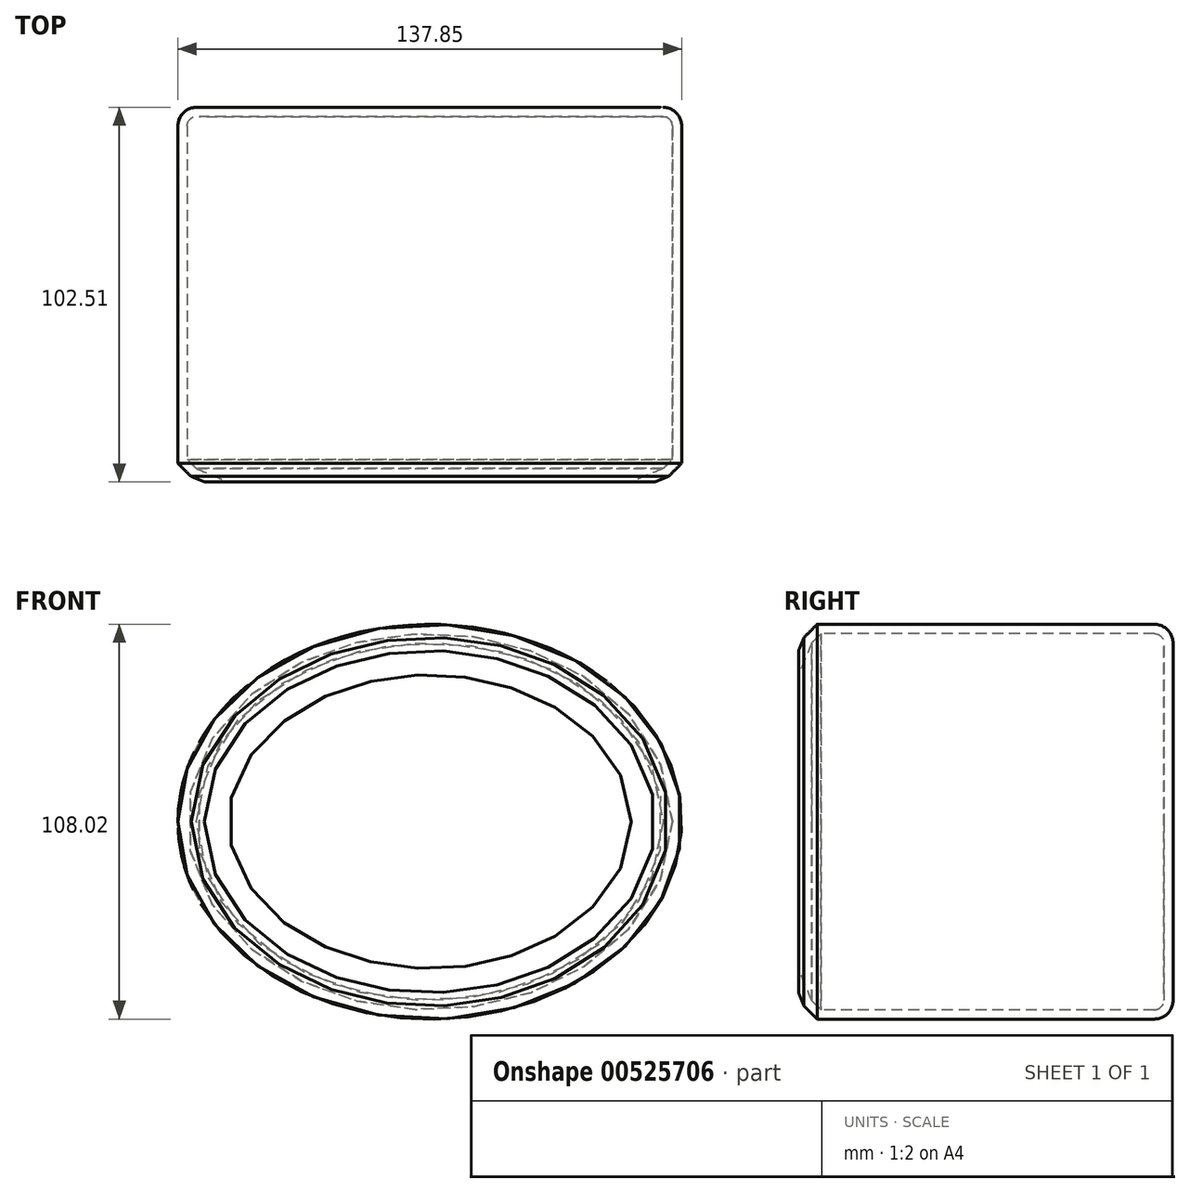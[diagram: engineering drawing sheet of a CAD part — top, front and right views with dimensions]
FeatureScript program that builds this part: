
annotation { "Feature Type Name" : "Feature", "Feature Type Description" : "" }
export const myFeature = defineFeature(function(context is Context, id is Id, definition is map)
    precondition{}
    {
        {
            var Q0;
            Q0=qCreatedBy(makeId("Front.planeOp"),FACE);
            var sketch = newSketch(context, id + "F0", { "sketchPlane" : qUnion([Q0])});
            skEllipse(sketch, "E0", {"center": v(0, 0) * mm, "majorRadius": 68.92 * mm, "minorRadius": 54 * mm, "majorAxis": v(-1, 0)});
            skSolve(sketch);
        }
        {
            var Q0;
            Q0=makeQuery(id+"F0.imprint","IMPRINT",FACE,{"disambiguationData":[TD([[makeQuery(id+"F0.imprint","IMPRINT",EDGE,{"derivedFrom":sQuery(id+"F0.wireOp",EDGE,"E0")}),1.0]])]});
            extrude(context, id + "F1", {"entities" : qUnion([Q0]), "depth" : 102.51 * mm, "offsetDistance" : 25.4 * mm});
        }
        {
            var Q0;
            Q0=makeQuery(id+"F1.opExtrude","CAP_FACE",FACE,{"disambiguationData":[OSD([sQuery(id+"F0.wireOp",EDGE,"E0")])],"isStart":false});
            var Q1;
            Q1=makeQuery(id+"F1.opExtrude","CAP_EDGE",EDGE,{"disambiguationData":[OSD([sQuery(id+"F0.wireOp",EDGE,"E0")])],"isStart":false});
            chamfer(context, id + "F2", {"entities" : qUnion([Q0, Q1]), "width" : 5.08 * mm, "tangentPropagation" : true});
        }
        {
            var Q0;
            Q0=makeQuery(id+"F1.opExtrude","CAP_FACE",FACE,{"disambiguationData":[OSD([sQuery(id+"F0.wireOp",EDGE,"E0")])],"isStart":false});
            chamfer(context, id + "F3", {"entities" : qUnion([Q0]), "width" : 5.08 * mm, "tangentPropagation" : true});
        }
        {
            var Q0;
            Q0=makeQuery(id+"F1.opExtrude","CAP_FACE",FACE,{"disambiguationData":[OSD([sQuery(id+"F0.wireOp",EDGE,"E0")])],"isStart":true});
            fillet(context, id + "F4", {"entities" : qUnion([Q0]), "radius" : 5.08 * mm, "tangentPropagation" : true, "allowEdgeOverflow" : false});
        }
        {
            var Q0;
            Q0=makeQuery(id+"F1.opExtrude","CAP_FACE",FACE,{"disambiguationData":[OSD([sQuery(id+"F0.wireOp",EDGE,"E0")])],"isStart":false});
            shell(context, id + "F5", {"entities" : qUnion([Q0]), "thickness" : 2.54 * mm});
        }
    });
